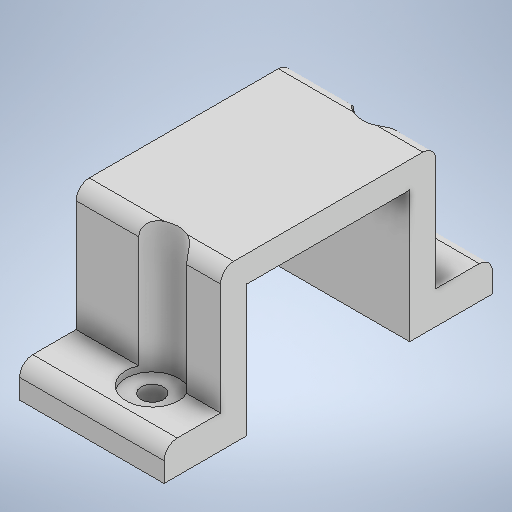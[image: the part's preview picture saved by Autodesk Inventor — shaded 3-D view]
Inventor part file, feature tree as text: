
AUTODESK INVENTOR PART (.ipt)
format: ipt  version: 2025 (Build 290162000, 162)  size: 308,224 bytes
history: native  units: mm
features: sketch x5, hole x3, extrude x2, fillet x2
ambient origin geometry x8: Origin, YZ Plane, XZ Plane, XY Plane, X Axis, Y Axis, Z Axis, Center Point
bodies: Solid1 (feature_tree)
feature tree (12):
  extrude  "Extrusion1"  Depth=6.3mm
  hole  "Hole1"  [1 undecoded]
  hole  "Hole2"  [1 undecoded]
  hole  "Hole3"  [1 undecoded]
  fillet  "Fillet1"  Radius=3.5mm
  extrude  "Extrusion2"  Depth=0.3mm
  fillet  "Fillet2"  Radius=3.5mm
  sketch  "Sketch1"  dims[d1=25.0mm d2=6.3mm]
  sketch  "Sketch2"  dims[d5=10.0mm d6=10.0mm]
  sketch  "Sketch3"  dims[d9=2.0mm d10=2.5mm]
  sketch  "Sketch4"  dims[d11=6.2mm d12=11.0mm d13=0.0mm d15=3.5mm]
  sketch  "Sketch5"  dims[d16=6.6mm d17=1.7mm d18=3.708mm d19=4.0mm d20=2.0mm d21=90.0deg d22=5.692mm d23=0.0mm d24=6.6mm d25=3.5mm d26=90.0deg d27=1.7mm d28=6.0mm d29=4.0mm d30=2.0mm d31=90.0deg d32=5.692mm d33=0.0mm d34=4.0mm d35=6.0mm d36=4.0mm d37=2.0mm d38=90.0deg d39=10.0mm d40=0.0mm d41=1.0mm d42=1.0mm d43=4.0mm d44=0.5mm d45=0.0mm d46=0.3mm]
note: 3 required parameter values undecoded (feature->parameter linkage not recoverable at this tier; creation-order binding heuristic only, values carry confidence <= 0.55)
